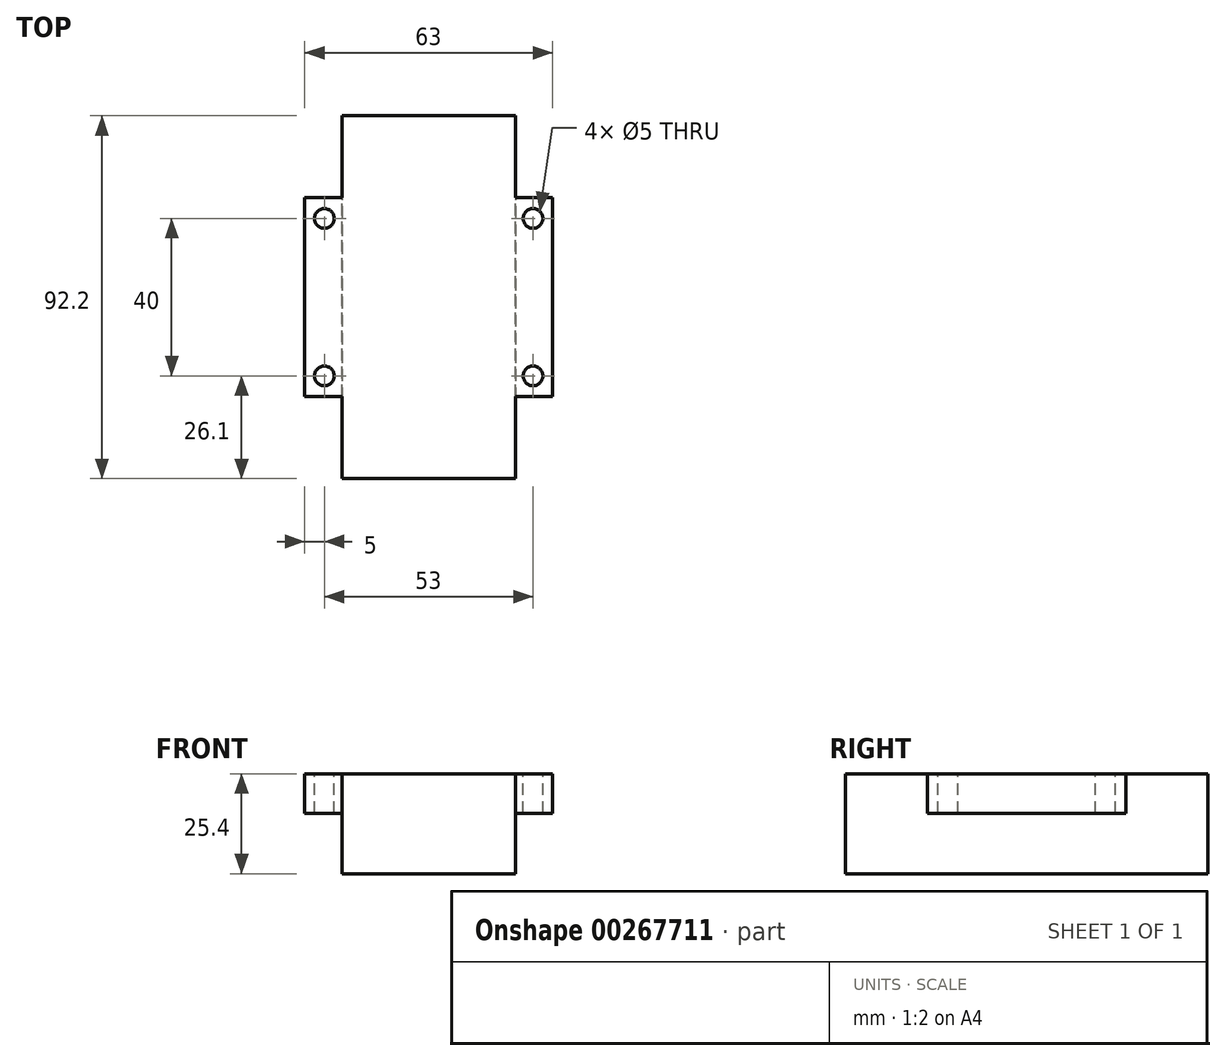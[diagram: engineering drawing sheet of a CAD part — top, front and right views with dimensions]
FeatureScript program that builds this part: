
annotation { "Feature Type Name" : "Feature", "Feature Type Description" : "" }
export const myFeature = defineFeature(function(context is Context, id is Id, definition is map)
    precondition{}
    {
        {
            var Q0;
            Q0=qCreatedBy(makeId("Front.planeOp"),FACE);
            var sketch = newSketch(context, id + "F0", { "sketchPlane" : qUnion([Q0])});
            skLineSegment(sketch, "E0.bottom", {"start": v(-22, 12.7) * mm, "end": v(22, 12.7) * mm});
            skLineSegment(sketch, "E0.top", {"start": v(-22, -12.7) * mm, "end": v(22, -12.7) * mm});
            skLineSegment(sketch, "E0.left", {"start": v(-22, 12.7) * mm, "end": v(-22, -12.7) * mm});
            skLineSegment(sketch, "E0.right", {"start": v(22, 12.7) * mm, "end": v(22, -12.7) * mm});
            skPoint(sketch, "E0.middle", {"position": v(0, 0) * mm});
            skSolve(sketch);
        }
        {
            var Q0;
            Q0=qSketchRegion(id+"F0",true);
            extrude(context, id + "F1", {"entities" : qUnion([Q0]), "oppositeDirection" : true, "depth" : 92.2 * mm});
        }
        {
            var Q0;
            Q0=makeQuery(id+"F1.opExtrude","SWEPT_FACE",FACE,{"disambiguationData":[OSD([sQuery(id+"F0.wireOp",EDGE,"E0.bottom")])]});
            var sketch = newSketch(context, id + "F2", { "sketchPlane" : qUnion([Q0])});
            skLineSegment(sketch, "E1.bottom", {"start": v(16, 118.22) * mm, "end": v(-16, 118.22) * mm, "construction": true});
            skLineSegment(sketch, "E1.top", {"start": v(16, -118.22) * mm, "end": v(-16, -118.22) * mm, "construction": true});
            skLineSegment(sketch, "E1.left", {"start": v(16, 118.22) * mm, "end": v(16, -118.22) * mm, "construction": true});
            skLineSegment(sketch, "E1.right", {"start": v(-16, 118.22) * mm, "end": v(-16, -118.22) * mm, "construction": true});
            skPoint(sketch, "E1.middle", {"position": v(0, 0) * mm});
            skLineSegment(sketch, "E2", {"start": v(-22, 46.1) * mm, "end": v(22, 46.1) * mm, "construction": true});
            skLineSegment(sketch, "E3.bottom", {"start": v(16, 64.1) * mm, "end": v(-25.34, 64.1) * mm, "construction": true});
            skLineSegment(sketch, "E3.top", {"start": v(16, 28.1) * mm, "end": v(-25.34, 28.1) * mm, "construction": true});
            skLineSegment(sketch, "E3.right", {"start": v(-25.34, 64.1) * mm, "end": v(-25.34, 28.1) * mm, "construction": true});
            skPoint(sketch, "E3.middle", {"position": v(-4.67, 46.1) * mm});
            skSolve(sketch);
        }
        {
            var Q0;
            Q0=makeQuery(id+"F1.opExtrude","SWEPT_FACE",FACE,{"disambiguationData":[OSD([sQuery(id+"F0.wireOp",EDGE,"E0.bottom")])]});
            var sketch = newSketch(context, id + "F3", { "sketchPlane" : qUnion([Q0])});
            skLineSegment(sketch, "E4.bottom", {"start": v(31.5, 71.35) * mm, "end": v(-31.5, 71.35) * mm});
            skLineSegment(sketch, "E4.top", {"start": v(31.5, 20.85) * mm, "end": v(-31.5, 20.85) * mm});
            skLineSegment(sketch, "E4.left", {"start": v(31.5, 71.35) * mm, "end": v(31.5, 20.85) * mm});
            skLineSegment(sketch, "E4.right", {"start": v(-31.5, 71.35) * mm, "end": v(-31.5, 20.85) * mm});
            skPoint(sketch, "E4.middle", {"position": v(0, 46.1) * mm});
            skLineSegment(sketch, "E5", {"start": v(0, 71.35) * mm, "end": v(-26.5, 71.35) * mm, "construction": true});
            skLineSegment(sketch, "E6", {"start": v(0, 71.35) * mm, "end": v(26.5, 71.35) * mm, "construction": true});
            skLineSegment(sketch, "E7", {"start": v(-26.5, 71.35) * mm, "end": v(-26.5, 20.85) * mm, "construction": true});
            skLineSegment(sketch, "E8", {"start": v(26.5, 71.35) * mm, "end": v(26.5, 20.85) * mm, "construction": true});
            skLineSegment(sketch, "E9", {"start": v(0, 46.1) * mm, "end": v(0, 66.1) * mm, "construction": true});
            skLineSegment(sketch, "E10", {"start": v(0, 46.1) * mm, "end": v(0, 26.1) * mm, "construction": true});
            skLineSegment(sketch, "E11", {"start": v(0, 66.1) * mm, "end": v(-26.5, 66.1) * mm, "construction": true});
            skLineSegment(sketch, "E12", {"start": v(-26.5, 66.1) * mm, "end": v(-26.5, 26.1) * mm, "construction": true});
            skCircle(sketch, "E13", {"center": v(-26.5, 66.1) * mm, "radius": 2.5 * mm});
            skCircle(sketch, "E14", {"center": v(-26.5, 26.1) * mm, "radius": 2.5 * mm});
            skCircle(sketch, "E15", {"center": v(26.5, 26.1) * mm, "radius": 2.5 * mm});
            skCircle(sketch, "E16", {"center": v(26.5, 66.1) * mm, "radius": 2.5 * mm});
            skPoint(sketch, "E16.centerSnap0", {"position": v(-13.25, 66.1) * mm});
            skSolve(sketch);
        }
        {
            var Q0;
            Q0=qSketchRegion(id+"F3",true);
            var Q1;
            {var subQ0=sQuery(id+"F0.wireOp",EDGE,"E0.bottom");Q1=makeQuery(id+"F2.imprint","IMPRINT",FACE,{"disambiguationData":[TD([[makeQuery(id+"F2.imprint","IMPRINT",EDGE,{"derivedFrom":makeQuery(id+"F1.opExtrude","CAP_EDGE",EDGE,{"disambiguationData":[OSD([subQ0])],"isStart":true})}),1.0]])]});}
            extrude(context, id + "F4", {"entities" : qUnion([Q0, Q1]), "operationType" : NewBodyOperationType.ADD, "oppositeDirection" : true, "depth" : 10 * mm});
        }
    });
